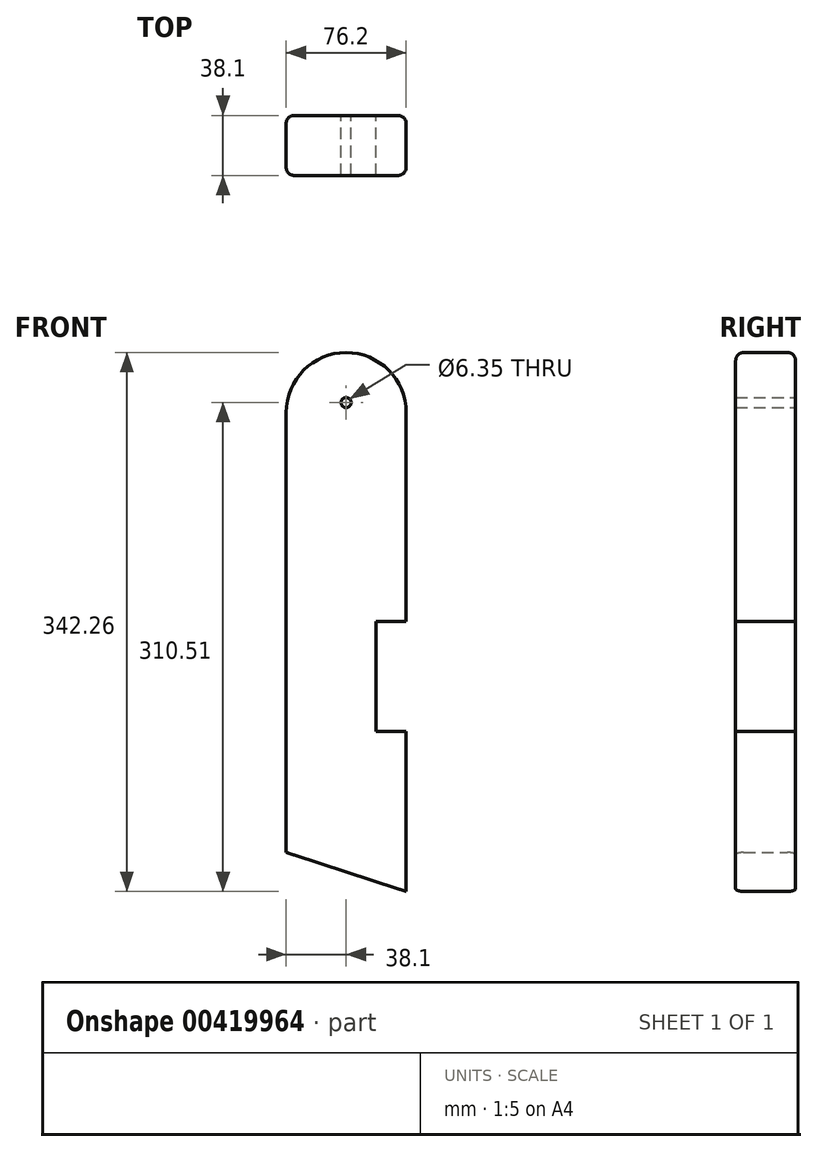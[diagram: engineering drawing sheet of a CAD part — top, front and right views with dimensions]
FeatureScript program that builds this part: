
annotation { "Feature Type Name" : "Feature", "Feature Type Description" : "" }
export const myFeature = defineFeature(function(context is Context, id is Id, definition is map)
    precondition{}
    {
        {
            var Q0;
            Q0=qCreatedBy(makeId("Front.planeOp"),FACE);
            var sketch = newSketch(context, id + "F0", { "sketchPlane" : qUnion([Q0])});
            skLineSegment(sketch, "E0", {"start": v(-38.1, 139.7) * mm, "end": v(-38.1, -139.7) * mm});
            skLineSegment(sketch, "E1", {"start": v(-38.1, -139.7) * mm, "end": v(38.1, -164.46) * mm});
            skLineSegment(sketch, "E2", {"start": v(38.1, -164.46) * mm, "end": v(38.1, 139.7) * mm});
            skArc(sketch, "E3", {"start": v(38.1, 139.7) * mm, "mid": v(0, 177.8) * mm, "end": v(-38.1, 139.7) * mm});
            skLineSegment(sketch, "E4", {"start": v(-38.1, 0) * mm, "end": v(38.1, 0) * mm, "construction": true});
            skPoint(sketch, "E5", {"position": v(0, 0) * mm});
            skLineSegment(sketch, "E6", {"start": v(0, -152.08) * mm, "end": v(0, 177.8) * mm, "construction": true});
            skLineSegment(sketch, "E7", {"start": v(-38.1, 139.7) * mm, "end": v(38.1, 139.7) * mm, "construction": true});
            skPoint(sketch, "E8", {"position": v(0, 146.05) * mm});
            skCircle(sketch, "E9", {"center": v(0, 146.05) * mm, "radius": 3.18 * mm});
            skLineSegment(sketch, "E10", {"start": v(38.1, 7) * mm, "end": v(19.05, 7) * mm});
            skLineSegment(sketch, "E11", {"start": v(19.05, 7) * mm, "end": v(19.05, -62.86) * mm});
            skLineSegment(sketch, "E12", {"start": v(19.05, -62.86) * mm, "end": v(38.1, -62.86) * mm});
            skSolve(sketch);
        }
        {
            var Q0;
            Q0=makeQuery(id+"F0.imprint","IMPRINT",FACE,{"disambiguationData":[TD([[makeQuery(id+"F0.imprint","IMPRINT",EDGE,{"derivedFrom":sQuery(id+"F0.wireOp",EDGE,"E0")}),1.0]])]});
            extrude(context, id + "F1", {"entities" : qUnion([Q0]), "depth" : 38.1 * mm});
        }
        {
            var Q0;
            Q0=makeQuery(id+"F1.opExtrude","CAP_EDGE",EDGE,{"disambiguationData":[OSD([sQuery(id+"F0.wireOp",EDGE,"E0")])],"isStart":true});
            var Q1;
            Q1=makeQuery(id+"F1.opExtrude","CAP_EDGE",EDGE,{"disambiguationData":[OSD([sQuery(id+"F0.wireOp",EDGE,"E2")])],"isStart":true});
            var Q2;
            Q2=makeQuery(id+"F1.opExtrude","CAP_EDGE",EDGE,{"disambiguationData":[OSD([sQuery(id+"F0.wireOp",EDGE,"E3")])],"isStart":true});
            var Q3;
            Q3=makeQuery(id+"F1.opExtrude","CAP_EDGE",EDGE,{"disambiguationData":[OSD([sQuery(id+"F0.wireOp",EDGE,"E0")])],"isStart":false});
            var Q4;
            Q4=makeQuery(id+"F1.opExtrude","CAP_EDGE",EDGE,{"disambiguationData":[OSD([sQuery(id+"F0.wireOp",EDGE,"E3")])],"isStart":false});
            var Q5;
            Q5=makeQuery(id+"F1.opExtrude","CAP_EDGE",EDGE,{"disambiguationData":[OSD([sQuery(id+"F0.wireOp",EDGE,"E2")])],"isStart":false});
            fillet(context, id + "F2", {"entities" : qUnion([Q0, Q1, Q2, Q3, Q4, Q5]), "radius" : 5.08 * mm, "tangentPropagation" : true, "allowEdgeOverflow" : false});
        }
        {
            var Q0;
            Q0=makeQuery(id+"F0.imprint","IMPRINT",FACE,{"disambiguationData":[TD([[makeQuery(id+"F0.imprint","IMPRINT",EDGE,{"derivedFrom":sQuery(id+"F0.wireOp",EDGE,"E9")}),1.0]])]});
            var Q1;
            Q1=sQuery(id+"F0.wireOp",EDGE,"E9");
            extrude(context, id + "F3", {"entities" : qUnion([Q0]), "operationType" : NewBodyOperationType.REMOVE, "surfaceEntities" : qUnion([Q1]), "oppositeDirection" : true, "depth" : 38.1 * mm});
        }
    });
